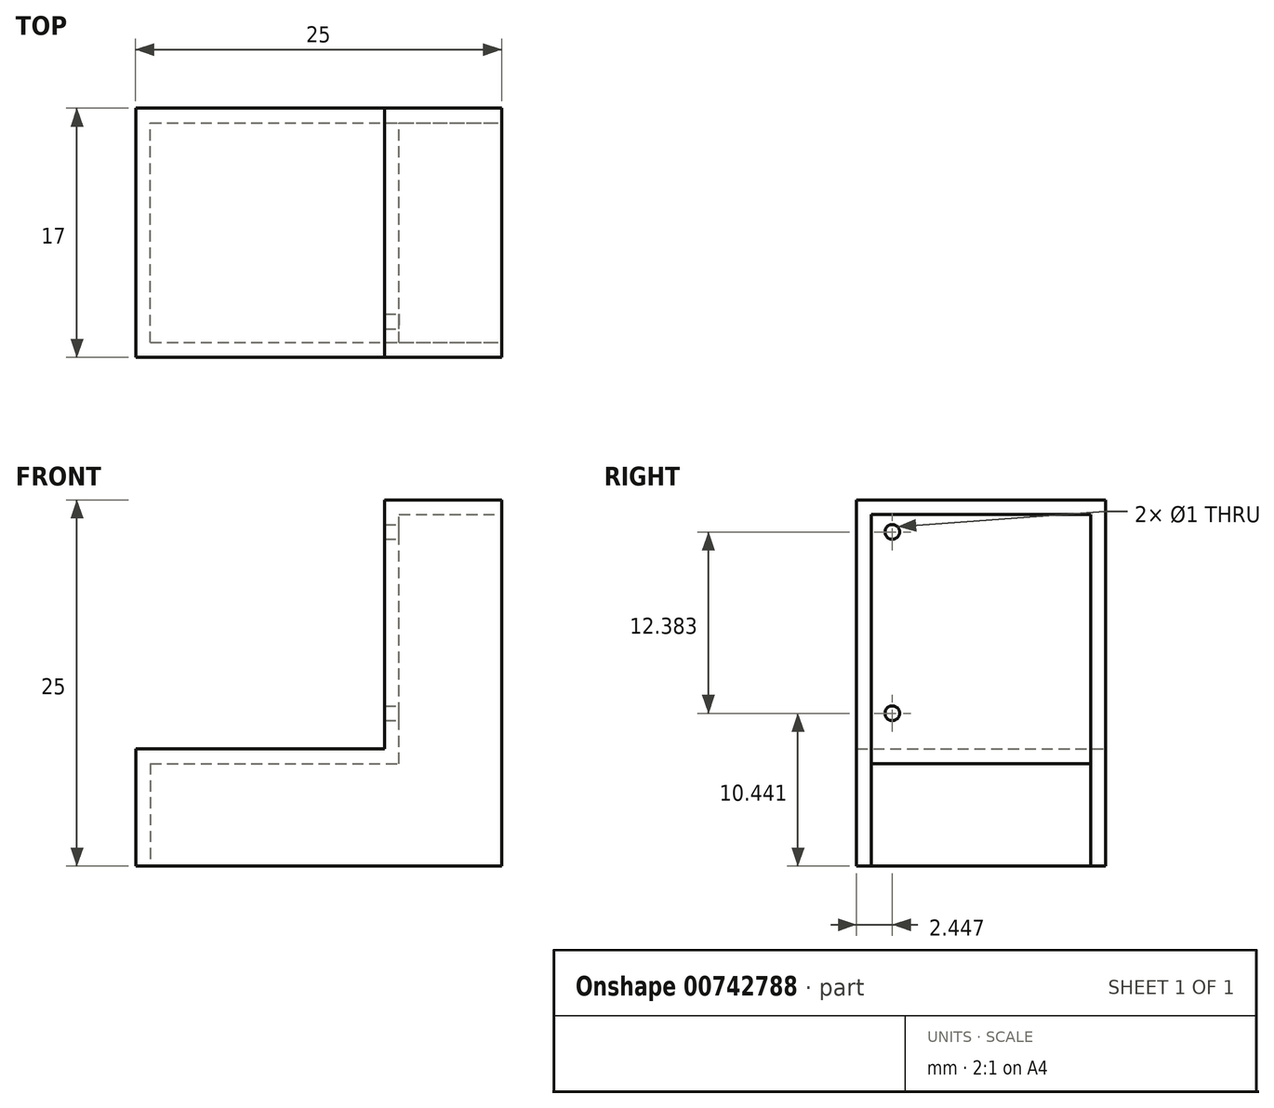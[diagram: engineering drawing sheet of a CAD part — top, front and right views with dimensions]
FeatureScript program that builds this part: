
annotation { "Feature Type Name" : "Feature", "Feature Type Description" : "" }
export const myFeature = defineFeature(function(context is Context, id is Id, definition is map)
    precondition{}
    {
        {
            var Q0;
            Q0=qCreatedBy(makeId("Front.planeOp"),FACE);
            var sketch = newSketch(context, id + "F0", { "sketchPlane" : qUnion([Q0])});
            skLineSegment(sketch, "E0.bottom", {"start": v(-60.16, 20.65) * mm, "end": v(-35.16, 20.65) * mm});
            skLineSegment(sketch, "E0.top", {"start": v(-60.16, 28.65) * mm, "end": v(-35.16, 28.65) * mm});
            skLineSegment(sketch, "E0.left", {"start": v(-60.16, 20.65) * mm, "end": v(-60.16, 28.65) * mm});
            skLineSegment(sketch, "E0.right", {"start": v(-35.16, 20.65) * mm, "end": v(-35.16, 28.65) * mm});
            skLineSegment(sketch, "E1.bottom", {"start": v(-43.16, 20.65) * mm, "end": v(-35.16, 20.65) * mm});
            skLineSegment(sketch, "E1.top", {"start": v(-43.16, 45.65) * mm, "end": v(-35.16, 45.65) * mm});
            skLineSegment(sketch, "E1.left", {"start": v(-43.16, 20.65) * mm, "end": v(-43.16, 45.65) * mm});
            skLineSegment(sketch, "E1.right", {"start": v(-35.16, 20.65) * mm, "end": v(-35.16, 45.65) * mm});
            skSolve(sketch);
        }
        {
            var Q0;
            {var subQ0=sQuery(id+"F0.wireOp",EDGE,"E0.bottom");Q0=makeQuery(id+"F0.imprint","IMPRINT",FACE,{"disambiguationData":[TD([[makeQuery(id+"F0.imprint","IMPRINT",EDGE,{"derivedFrom":subQ0}),1.0]])]});}
            var Q1;
            {var subQ5=sQuery(id+"F0.wireOp",EDGE,"E1.top");Q1=makeQuery(id+"F0.imprint","IMPRINT",FACE,{"disambiguationData":[TD([[makeQuery(id+"F0.imprint","IMPRINT",EDGE,{"derivedFrom":subQ5}),-1.0]])]});}
            var Q2;
            {var subQ5=sQuery(id+"F0.wireOp",EDGE,"E1.bottom");Q2=makeQuery(id+"F0.imprint","IMPRINT",FACE,{"disambiguationData":[TD([[makeQuery(id+"F0.imprint","IMPRINT",EDGE,{"derivedFrom":subQ5}),1.0]])]});}
            extrude(context, id + "F1", {"entities" : qUnion([Q0, Q1, Q2]), "depth" : 17 * mm, "offsetDistance" : 25 * mm});
        }
        {
            var Q0;
            Q0=makeQuery(id+"F1.opExtrude","SWEPT_FACE",FACE,{"disambiguationData":[OSD([sQuery(id+"F0.wireOp",EDGE,"E0.bottom"),sQuery(id+"F0.wireOp",EDGE,"E1.bottom")])]});
            var sketch = newSketch(context, id + "F2", { "sketchPlane" : qUnion([Q0])});
            skLineSegment(sketch, "E2.bottom", {"start": v(-59.16, 16) * mm, "end": v(-35.16, 16) * mm});
            skLineSegment(sketch, "E2.top", {"start": v(-59.16, 1) * mm, "end": v(-35.16, 1) * mm});
            skLineSegment(sketch, "E2.left", {"start": v(-59.16, 16) * mm, "end": v(-59.16, 1) * mm});
            skLineSegment(sketch, "E2.right", {"start": v(-35.16, 16) * mm, "end": v(-35.16, 1) * mm});
            skSolve(sketch);
        }
        {
            var Q0;
            Q0=makeQuery(id+"F2.imprint","IMPRINT",FACE,{"disambiguationData":[TD([[makeQuery(id+"F2.imprint","IMPRINT",EDGE,{"derivedFrom":sQuery(id+"F2.wireOp",EDGE,"E2.bottom")}),-1.0]])]});
            extrude(context, id + "F3", {"entities" : qUnion([Q0]), "operationType" : NewBodyOperationType.REMOVE, "oppositeDirection" : true, "depth" : 7 * mm, "offsetDistance" : 25 * mm});
        }
        {
            var Q0;
            Q0=makeQuery(id+"F1.opExtrude","SWEPT_FACE",FACE,{"disambiguationData":[OSD([sQuery(id+"F0.wireOp",EDGE,"E1.right")])]});
            var sketch = newSketch(context, id + "F4", { "sketchPlane" : qUnion([Q0])});
            skLineSegment(sketch, "E3.bottom", {"start": v(-16, 27.65) * mm, "end": v(-1, 27.65) * mm});
            skLineSegment(sketch, "E3.top", {"start": v(-16, 44.65) * mm, "end": v(-1, 44.65) * mm});
            skLineSegment(sketch, "E3.left", {"start": v(-16, 27.65) * mm, "end": v(-16, 44.65) * mm});
            skLineSegment(sketch, "E3.right", {"start": v(-1, 27.65) * mm, "end": v(-1, 44.65) * mm});
            skSolve(sketch);
        }
        {
            var Q0;
            Q0=makeQuery(id+"F4.imprint","IMPRINT",FACE,{"disambiguationData":[TD([[makeQuery(id+"F4.imprint","IMPRINT",EDGE,{"derivedFrom":sQuery(id+"F4.wireOp",EDGE,"E3.bottom")}),1.0]])]});
            extrude(context, id + "F5", {"entities" : qUnion([Q0]), "operationType" : NewBodyOperationType.REMOVE, "oppositeDirection" : true, "depth" : 7 * mm, "offsetDistance" : 25 * mm});
        }
        {
            var Q0;
            Q0=makeQuery(id+"F5.boolean.opBoolean","COPY",FACE,{"derivedFrom":makeQuery(id+"F5.opExtrude","CAP_FACE",FACE,{"disambiguationData":[OSD([sQuery(id+"F4.wireOp",EDGE,"E3.bottom"),sQuery(id+"F4.wireOp",EDGE,"E3.top"),sQuery(id+"F4.wireOp",EDGE,"E3.left"),sQuery(id+"F4.wireOp",EDGE,"E3.right")])],"isStart":false})});
            var sketch = newSketch(context, id + "F6", { "sketchPlane" : qUnion([Q0])});
            skCircle(sketch, "E4", {"center": v(-14.55, 31.1) * mm, "radius": 0.5 * mm});
            skCircle(sketch, "E5", {"center": v(-14.55, 43.47) * mm, "radius": 0.5 * mm});
            skSolve(sketch);
        }
        {
            var Q0;
            Q0=sQuery(id+"F6.wireOp",VERTEX,"E4.center");
            var Q1;
            Q1=sQuery(id+"F6.wireOp",VERTEX,"E5.center");
            var Q2;
            Q2=makeQuery(id+"F1.opExtrude","SWEPT_BODY",BODY,{"disambiguationData":[OSD([sQuery(id+"F0.wireOp",EDGE,"E0.bottom"),sQuery(id+"F0.wireOp",EDGE,"E0.top"),sQuery(id+"F0.wireOp",EDGE,"E0.left"),sQuery(id+"F0.wireOp",EDGE,"E1.bottom"),sQuery(id+"F0.wireOp",EDGE,"E1.top"),sQuery(id+"F0.wireOp",EDGE,"E1.left"),sQuery(id+"F0.wireOp",EDGE,"E1.right")])]});
            hole(context, id + "F7", {"style" : HoleStyle.SIMPLE, "endStyle" : HoleEndStyle.THROUGH, "holeDiameter" : 1 * mm, "majorDiameter" : 5 * mm, "isTappedThrough" : true, "tappedDepth" : 12 * mm, "tapClearance" : 3, "locations" : qUnion([Q0, Q1]), "scope" : qUnion([Q2])});
        }
    });
